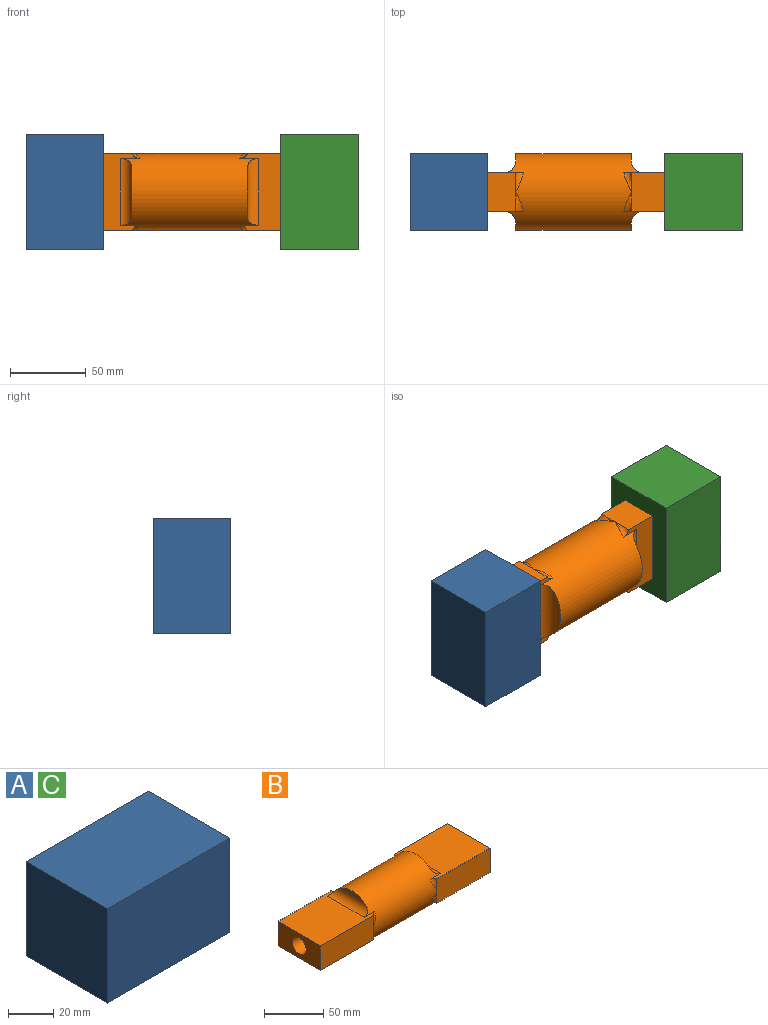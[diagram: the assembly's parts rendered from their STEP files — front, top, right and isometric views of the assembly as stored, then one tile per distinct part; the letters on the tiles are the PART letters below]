
ASSEMBLY  parts=3 mates=3
PART A: 11 faces, bbox 76.2x50.8x50.8 mm
  f0: plane 50.8x25.4mm, normal (0,1,0), area 1290.3mm2, adj f1,f7,f8,f9
  f1: plane 25.4x25.4mm, normal (1,0,0), area 645.2mm2, adj f0,f2,f8,f9
  f2: plane 50.8x25.4mm, normal (0,-1,0), area 1290.3mm2, adj f1,f7,f8,f9
  f3: plane 76.2x50.8mm, normal (0,1,0), area 3871mm2, adj f4,f6,f8,f10
  f4: plane 50.8x50.8mm, normal (-1,0,0), area 2580.6mm2, adj f3,f5,f8,f10
  f5: plane 76.2x50.8mm, normal (0,-1,0), area 3871mm2, adj f4,f6,f8,f10
  f6: plane 50.8x50.8mm, normal (1,0,0), area 2580.6mm2, adj f3,f5,f8,f10
  f7: plane 25.4x25.4mm, normal (-1,0,0), area 645.2mm2, adj f0,f2,f8,f9
  f8: plane 76.2x50.8mm, normal (0,0,-1), area 2580.6mm2, adj f0,f1,f2,f3,f4,f5,f6,f7
  f9: plane 50.8x25.4mm, normal (0,0,-1), area 1290.3mm2, adj f0,f1,f2,f7
  f10: plane 76.2x50.8mm, normal (0,0,1), area 3871mm2, adj f3,f4,f5,f6
PART B: 31 faces, bbox 206x53.6x53.6 mm
  f0: plane 66.3x28.2mm, normal (0,-1,0), area 1612.9mm2, adj f1,f3,f5,f13,f14
  f1: plane 69.21x51.53mm, normal (0,0,-1), area 2900.7mm2, adj f0,f2,f5,f7,f11,f12,f13
  f2: plane 66.3x28.2mm, normal (0,1,0), area 1612.9mm2, adj f1,f3,f5,f12,f15
  f3: plane 69.2x51.52mm, normal (0,0,1), area 2900.7mm2, adj f0,f2,f5,f7,f10,f14,f15
  f4: cylinder r=8.3mm len=63.5mm, axis (-1,0,0), area 3310.2mm2, adj f5,f9
  f5: plane 50.8x25.4mm, normal (-1,0,0), area 1074.1mm2, adj f0,f1,f2,f3,f4
  f6: plane 30.48x5.08mm, normal (-1,0,0), area 105.5mm2, adj f7,f11
  f7: cylinder r=25.4mm len=91.44mm, axis (-1,0,0), area 12208.5mm2, adj f1,f3,f6,f8,f10,f11,f12,f13
  f8: plane 30.48x5.08mm, normal (-1,0,0), area 105.5mm2, adj f7,f10
  f9: revolved ~38.1x38.1mm, area 4597.3mm2, adj f4,f24
  f10: cylinder r=7.62mm len=43.99mm, axis (0,1,0), area 445.7mm2, adj f3,f7,f8
  f11: cylinder r=7.62mm len=43.99mm, axis (0,-1,0), area 445.7mm2, adj f1,f6,f7
  f12: bspline ~15.85x5.04mm, area 29.1mm2, adj f1,f2,f7
  f13: bspline ~15.85x5.04mm, area 29.1mm2, adj f0,f1,f7
  f14: bspline ~15.85x5.04mm, area 29.1mm2, adj f0,f3,f7
  f15: bspline ~15.85x5.04mm, area 29.1mm2, adj f2,f3,f7
  f16: plane 66.3x28.2mm, normal (0,-1,0), area 1612.9mm2, adj f17,f19,f21,f28,f29
  f17: plane 69.21x51.53mm, normal (0,0,-1), area 2900.7mm2, adj f7,f16,f18,f21,f26,f27,f28
  f18: plane 66.3x28.2mm, normal (0,1,0), area 1612.9mm2, adj f17,f19,f21,f27,f30
  f19: plane 69.2x51.52mm, normal (0,0,1), area 2900.7mm2, adj f7,f16,f18,f21,f25,f29,f30
  f20: cylinder r=8.3mm len=63.5mm, axis (1,0,0), area 3310.2mm2, adj f21,f24
  f21: plane 50.8x25.4mm, normal (1,0,0), area 1074.1mm2, adj f16,f17,f18,f19,f20
  f22: plane 30.48x5.08mm, normal (1,0,0), area 105.5mm2, adj f7,f26
  f23: plane 30.48x5.08mm, normal (1,0,0), area 105.5mm2, adj f7,f25
  f24: revolved ~38.1x38.1mm, area 4597.3mm2, adj f9,f20
  f25: cylinder r=7.62mm len=43.99mm, axis (0,1,0), area 445.7mm2, adj f7,f19,f23
  f26: cylinder r=7.62mm len=43.99mm, axis (0,-1,0), area 445.7mm2, adj f7,f17,f22
  f27: bspline ~15.85x5.04mm, area 29.1mm2, adj f7,f17,f18
  f28: bspline ~15.85x5.04mm, area 29.1mm2, adj f7,f16,f17
  f29: bspline ~15.85x5.04mm, area 29.1mm2, adj f7,f16,f19
  f30: bspline ~15.85x5.04mm, area 29.1mm2, adj f7,f18,f19
PART C: same geometry as A
PLACE A rot(axis=(0.71,0,-0.71),180deg) t=(-14.56,19.81,27.11)mm
PLACE B rot(axis=(1,0,0),90deg) t=(-59.01,19.81,-23.69)mm
PLACE C rot(axis=(0.71,0,0.71),180deg) t=(102.85,19.81,-23.69)mm
MATE fastened B.f17 <-> C.f0  axis (0,1,0) through (115.55,19.81,1.71)mm
MATE fastened C.f9 <-> B.f4  axis (-1,0,0) through (128.25,7.11,1.71)mm
MATE fastened A.f1 <-> B.f2  axis (0,0,-1) through (-27.26,7.11,27.11)mm
